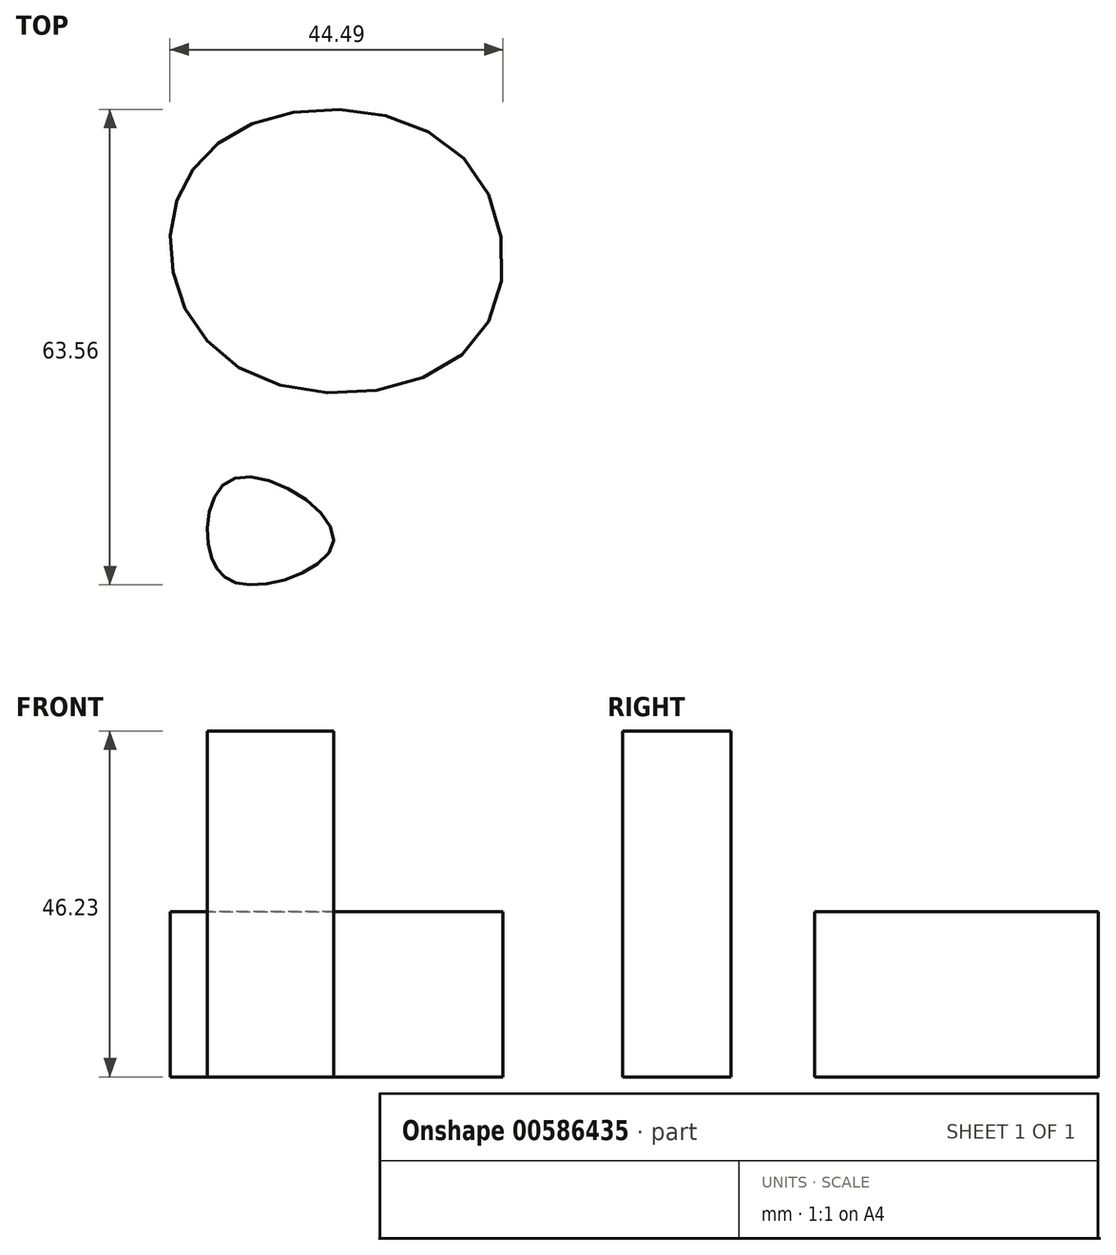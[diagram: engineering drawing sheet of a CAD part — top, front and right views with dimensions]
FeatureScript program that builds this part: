
annotation { "Feature Type Name" : "Feature", "Feature Type Description" : "" }
export const myFeature = defineFeature(function(context is Context, id is Id, definition is map)
    precondition{}
    {
        {
            var Q0;
            Q0=qCreatedBy(makeId("Top.planeOp"),FACE);
            var sketch = newSketch(context, id + "F0", { "sketchPlane" : qUnion([Q0])});
            skFitSpline(sketch, "E0", {"points": [v(-48.2, 24.96) * mm, v(-37.34, 39.85) * mm, v(-9.16, 35.43) * mm, v(-7.55, 10.67) * mm, v(-37.54, 6.44) * mm, v(-48.2, 24.96) * mm]});
            skSolve(sketch);
        }
        {
            var Q0;
            Q0 = qSketchRegion(id + "F0", true);
            extrude(context, id + "F1", {"entities" : qUnion([Q0]), "depth" : 22.1 * mm, "offsetDistance" : 25.4 * mm});
        }
        {
            var Q0;
            Q0=qCreatedBy(makeId("Top.planeOp"),FACE);
            var sketch = newSketch(context, id + "F2", { "sketchPlane" : qUnion([Q0])});
            skFitSpline(sketch, "E1", {"points": [v(-37.58, -21.76) * mm, v(-43, -16.97) * mm, v(-39.35, -7.44) * mm, v(-26.39, -15.53) * mm, v(-37.58, -21.76) * mm]});
            skSolve(sketch);
        }
        {
            var Q0;
            Q0=makeQuery(id+"F2.imprint","IMPRINT",FACE,{"disambiguationData":[TD([[makeQuery(id+"F2.imprint","IMPRINT",EDGE,{"derivedFrom":sQuery(id+"F2.wireOp",EDGE,"E1")}),-1.0]])]});
            var Q1;
            Q1=sQuery(id+"F2.wireOp",EDGE,"E1");
            extrude(context, id + "F3", {"entities" : qUnion([Q0]), "surfaceEntities" : qUnion([Q1]), "depth" : 46.23 * mm, "offsetDistance" : 25.4 * mm});
        }
    });
